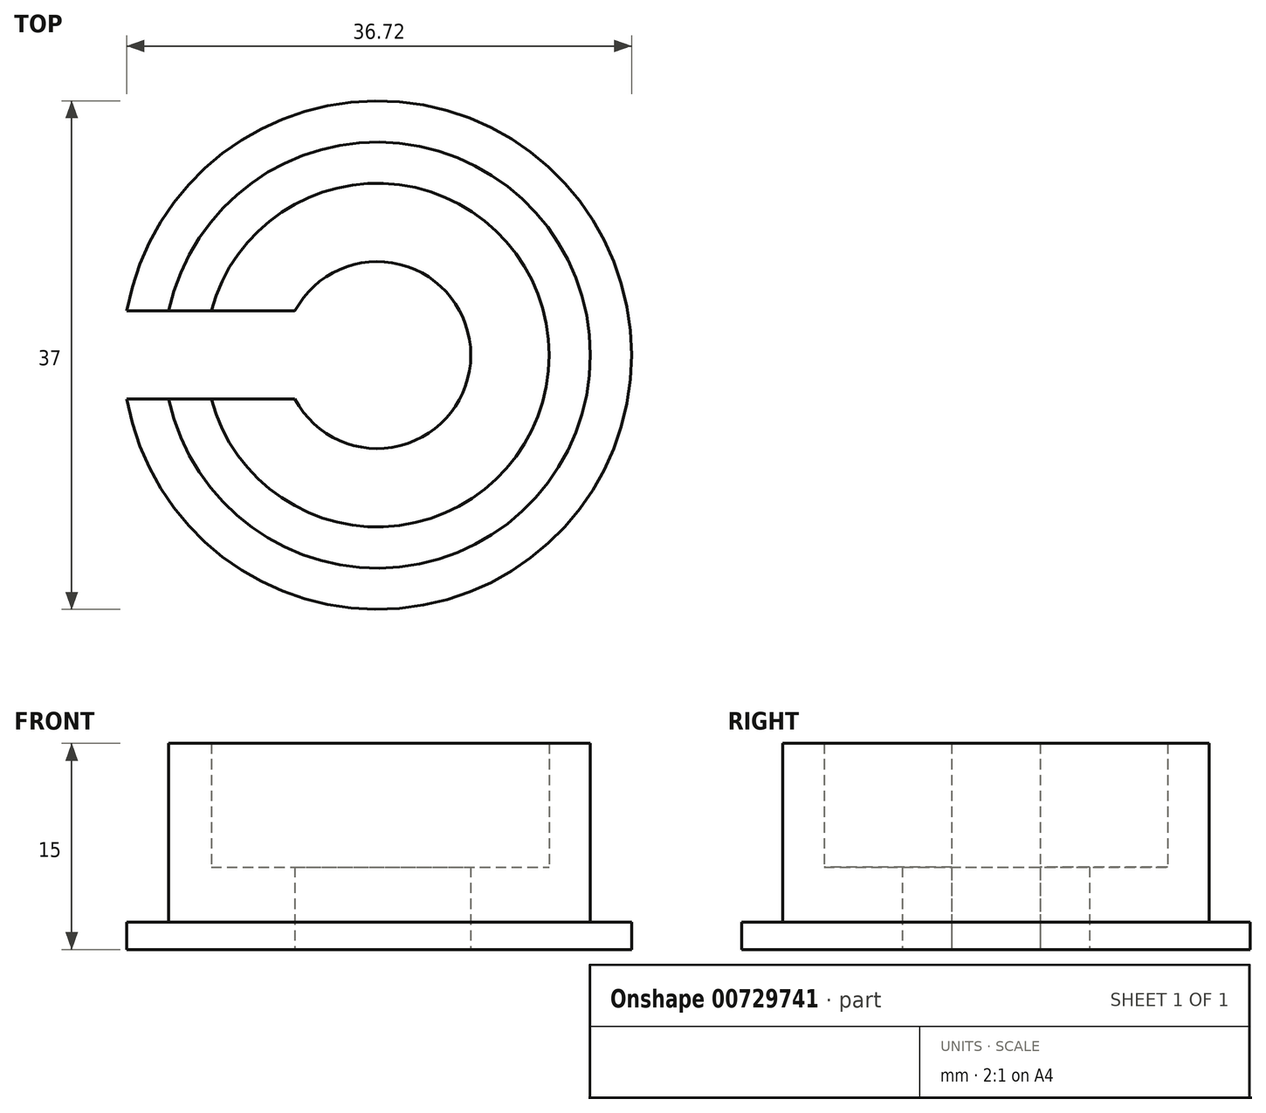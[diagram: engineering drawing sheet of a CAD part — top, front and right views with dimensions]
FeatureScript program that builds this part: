
annotation { "Feature Type Name" : "Feature", "Feature Type Description" : "" }
export const myFeature = defineFeature(function(context is Context, id is Id, definition is map)
    precondition{}
    {
        {
            var Q0;
            Q0=qCreatedBy(makeId("Top.planeOp"),FACE);
            var sketch = newSketch(context, id + "F0", { "sketchPlane" : qUnion([Q0])});
            skCircle(sketch, "E0", {"center": v(0, 0) * mm, "radius": 6.8 * mm});
            skCircle(sketch, "E1", {"center": v(0, 0) * mm, "radius": 15.5 * mm});
            skCircle(sketch, "E2", {"center": v(0, 0) * mm, "radius": 18.5 * mm});
            skCircle(sketch, "E3", {"center": v(0, 0) * mm, "radius": 12.5 * mm});
            skLineSegment(sketch, "E4.bottom", {"start": v(-3.59, -3.2) * mm, "end": v(-24.59, -3.2) * mm});
            skLineSegment(sketch, "E4.top", {"start": v(-3.59, 3.2) * mm, "end": v(-24.59, 3.2) * mm});
            skLineSegment(sketch, "E4.left", {"start": v(-3.59, -3.2) * mm, "end": v(-3.59, 3.2) * mm});
            skLineSegment(sketch, "E4.right", {"start": v(-24.59, -3.2) * mm, "end": v(-24.59, 3.2) * mm});
            skPoint(sketch, "E4.middle", {"position": v(-14.09, 0) * mm});
            skSolve(sketch);
        }
        {
            var Q0;
            Q0=makeQuery(id+"F0.imprint","IMPRINT",FACE,{"disambiguationData":[TD([[makeQuery(id+"F0.imprint","IMPRINT",EDGE,{"derivedFrom":sQuery(id+"F0.wireOp",EDGE,"E1")}),-1.0]])]});
            extrude(context, id + "F1", {"entities" : qUnion([Q0]), "depth" : 2 * mm, "offsetDistance" : 25 * mm});
        }
        {
            var Q0;
            Q0=makeQuery(id+"F0.imprint","IMPRINT",FACE,{"disambiguationData":[TD([[makeQuery(id+"F0.imprint","IMPRINT",EDGE,{"derivedFrom":sQuery(id+"F0.wireOp",EDGE,"E1")}),1.0]])]});
            extrude(context, id + "F2", {"entities" : qUnion([Q0]), "operationType" : NewBodyOperationType.ADD, "depth" : 15 * mm, "offsetDistance" : 25 * mm});
        }
        {
            var Q0;
            Q0=makeQuery(id+"F0.imprint","IMPRINT",FACE,{"disambiguationData":[TD([[makeQuery(id+"F0.imprint","IMPRINT",EDGE,{"derivedFrom":sQuery(id+"F0.wireOp",EDGE,"E0")}),-1.0]])]});
            extrude(context, id + "F3", {"entities" : qUnion([Q0]), "operationType" : NewBodyOperationType.ADD, "depth" : 6 * mm, "offsetDistance" : 25 * mm});
        }
        {
            var Q0;
            {var subQ5=sQuery(id+"F0.wireOp",EDGE,"E4.right");Q0=makeQuery(id+"F0.imprint","IMPRINT",FACE,{"disambiguationData":[TD([[makeQuery(id+"F0.imprint","IMPRINT",EDGE,{"derivedFrom":subQ5}),-1.0]])]});}
            var Q1;
            {var subQ0=sQuery(id+"F0.wireOp",EDGE,"E4.bottom");var subQ1=sQuery(id+"F0.wireOp",EDGE,"E0");var subQ2=makeQuery(id+"F0.imprint","INTERSECT",VERTEX,{"derivedFrom":[subQ1,subQ0]});Q1=makeQuery(id+"F0.imprint","IMPRINT",FACE,{"disambiguationData":[TD([[makeQuery(id+"F0.imprint","IMPRINT",EDGE,{"disambiguationData":[TD([[subQ2,1.0]])],"derivedFrom":subQ1}),-1.0]])]});}
            var Q2;
            {var subQ0=sQuery(id+"F0.wireOp",EDGE,"E4.bottom");var subQ1=sQuery(id+"F0.wireOp",EDGE,"E1");var subQ2=makeQuery(id+"F0.imprint","INTERSECT",VERTEX,{"derivedFrom":[subQ1,subQ0]});Q2=makeQuery(id+"F0.imprint","IMPRINT",FACE,{"disambiguationData":[TD([[makeQuery(id+"F0.imprint","IMPRINT",EDGE,{"disambiguationData":[TD([[subQ2,1.0]])],"derivedFrom":subQ1}),-1.0]])]});}
            var Q3;
            {var subQ0=sQuery(id+"F0.wireOp",EDGE,"E4.bottom");var subQ1=sQuery(id+"F0.wireOp",EDGE,"E1");var subQ2=makeQuery(id+"F0.imprint","INTERSECT",VERTEX,{"derivedFrom":[subQ1,subQ0]});Q3=makeQuery(id+"F0.imprint","IMPRINT",FACE,{"disambiguationData":[TD([[makeQuery(id+"F0.imprint","IMPRINT",EDGE,{"disambiguationData":[TD([[subQ2,1.0]])],"derivedFrom":subQ1}),1.0]])]});}
            extrude(context, id + "F4", {"entities" : qUnion([Q0, Q1, Q2, Q3]), "operationType" : NewBodyOperationType.REMOVE, "depth" : 23.4 * mm, "offsetDistance" : 25 * mm});
        }
    });
